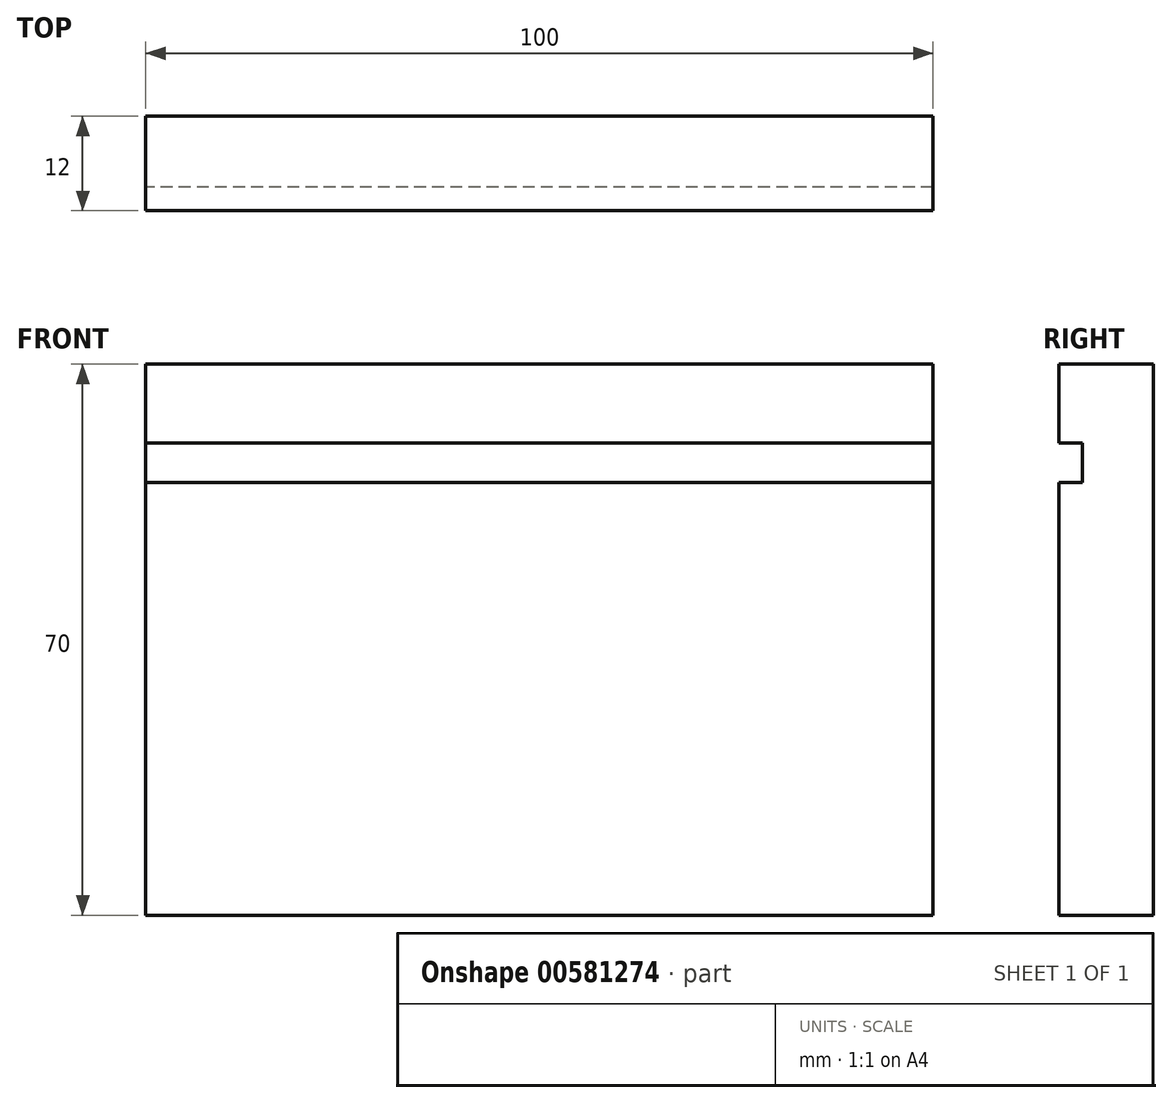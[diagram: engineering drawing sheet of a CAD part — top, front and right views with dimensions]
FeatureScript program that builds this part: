
annotation { "Feature Type Name" : "Feature", "Feature Type Description" : "" }
export const myFeature = defineFeature(function(context is Context, id is Id, definition is map)
    precondition{}
    {
        {
            var Q0;
            Q0=qCreatedBy(makeId("Right.planeOp"),FACE);
            var sketch = newSketch(context, id + "F0", { "sketchPlane" : qUnion([Q0])});
            skLineSegment(sketch, "E0", {"start": v(0, 0) * mm, "end": v(0, 70) * mm});
            skLineSegment(sketch, "E1", {"start": v(0, 70) * mm, "end": v(-12, 70) * mm});
            skLineSegment(sketch, "E2", {"start": v(-12, 70) * mm, "end": v(-12, 60) * mm});
            skLineSegment(sketch, "E3", {"start": v(-12, 60) * mm, "end": v(-9, 60) * mm});
            skLineSegment(sketch, "E4", {"start": v(-9, 60) * mm, "end": v(-9, 55) * mm});
            skLineSegment(sketch, "E5", {"start": v(-9, 55) * mm, "end": v(-12, 55) * mm});
            skLineSegment(sketch, "E6", {"start": v(-12, 55) * mm, "end": v(-12, 0) * mm});
            skLineSegment(sketch, "E7", {"start": v(-12, 0) * mm, "end": v(0, 0) * mm});
            skSolve(sketch);
        }
        {
            var Q0;
            Q0 = qSketchRegion(id + "F0", true);
            extrude(context, id + "F1", {"entities" : qUnion([Q0]), "depth" : 900 * mm, "offsetDistance" : 25 * mm});
        }
        {
            var Q0;
            Q0=makeQuery(id+"F1.opExtrude","SWEPT_FACE",FACE,{"disambiguationData":[OSD([sQuery(id+"F0.wireOp",EDGE,"E6")])]});
            var sketch = newSketch(context, id + "F2", { "sketchPlane" : qUnion([Q0])});
            skLineSegment(sketch, "E8.bottom", {"start": v(900, 0) * mm, "end": v(100, 0) * mm});
            skLineSegment(sketch, "E8.top", {"start": v(900, 435.55) * mm, "end": v(100, 435.55) * mm});
            skLineSegment(sketch, "E8.left", {"start": v(900, 0) * mm, "end": v(900, 435.55) * mm});
            skLineSegment(sketch, "E8.right", {"start": v(100, 0) * mm, "end": v(100, 435.55) * mm});
            skSolve(sketch);
        }
        {
            var Q0;
            Q0 = qSketchRegion(id + "F2", true);
            extrude(context, id + "F3", {"entities" : qUnion([Q0]), "operationType" : NewBodyOperationType.REMOVE, "oppositeDirection" : true, "depth" : 25 * mm, "offsetDistance" : 25 * mm});
        }
    });
